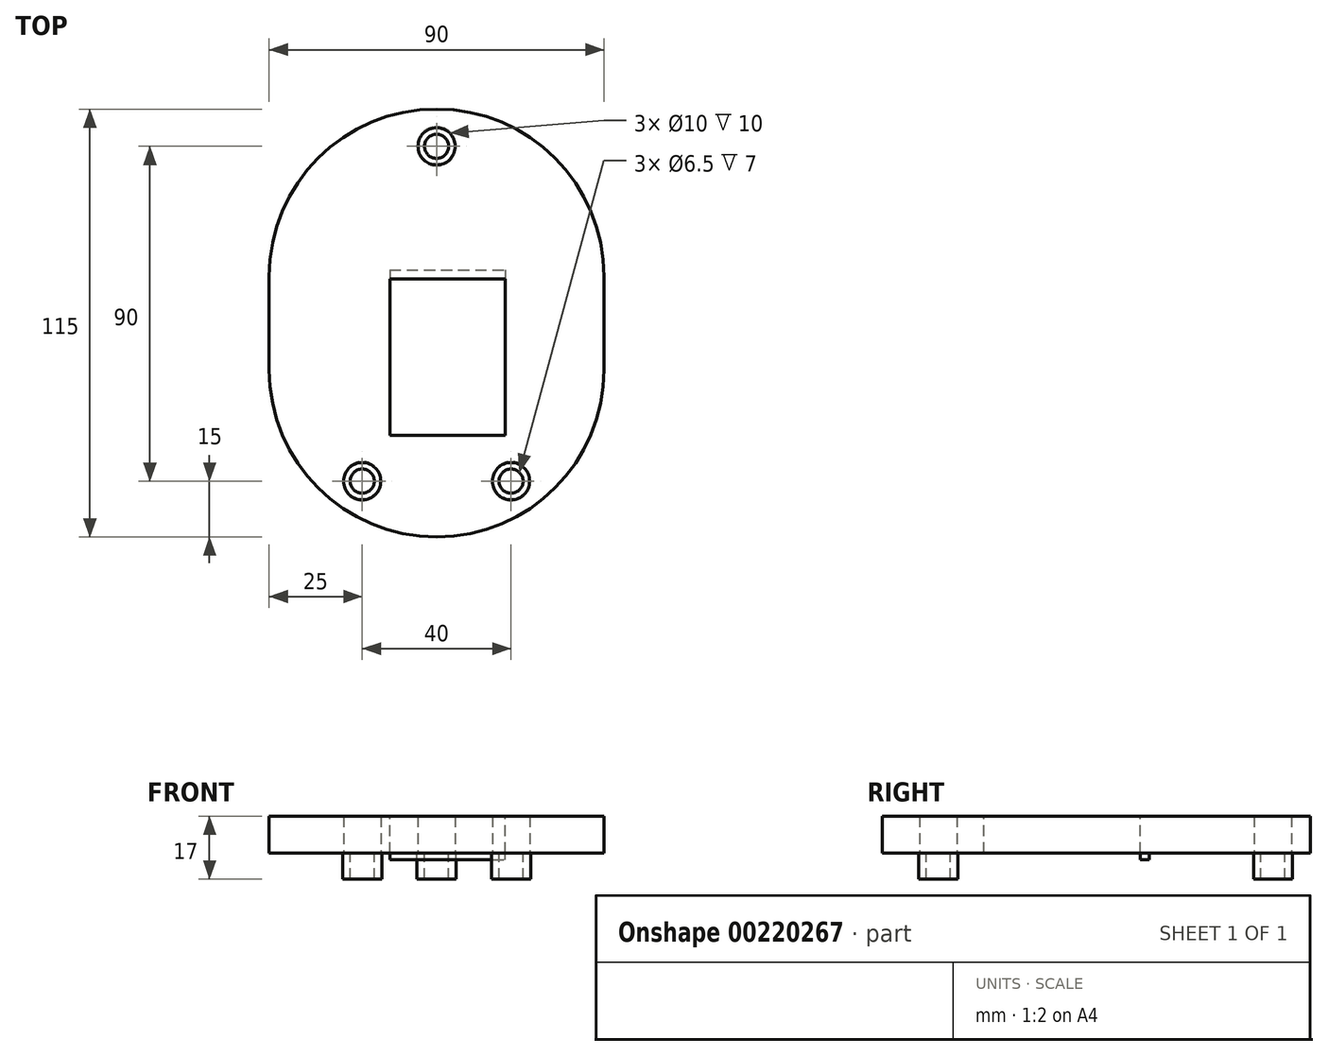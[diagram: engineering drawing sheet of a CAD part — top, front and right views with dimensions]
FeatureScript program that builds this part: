
annotation { "Feature Type Name" : "Feature", "Feature Type Description" : "" }
export const myFeature = defineFeature(function(context is Context, id is Id, definition is map)
    precondition{}
    {
        {
            var Q0;
            Q0=qCreatedBy(makeId("Top.planeOp"),FACE);
            var sketch = newSketch(context, id + "F0", { "sketchPlane" : qUnion([Q0])});
            skArc(sketch, "E0", {"start": v(-45, 0) * mm, "mid": v(0, -45) * mm, "end": v(45, 0) * mm});
            skLineSegment(sketch, "E1", {"start": v(-45, 0) * mm, "end": v(-45, 70) * mm});
            skLineSegment(sketch, "E2", {"start": v(-45, 70) * mm, "end": v(45, 70) * mm});
            skLineSegment(sketch, "E3", {"start": v(45, 70) * mm, "end": v(45, 0) * mm});
            skSolve(sketch);
        }
        {
            var Q0;
            Q0=qSketchRegion(id+"F0",true);
            extrude(context, id + "F1", {"entities" : qUnion([Q0]), "depth" : 10 * mm});
        }
        {
            var Q0;
            Q0=makeQuery(id+"F1.opExtrude","CAP_FACE",FACE,{"disambiguationData":[OSD([sQuery(id+"F0.wireOp",EDGE,"E0")])],"isStart":true});
            var sketch = newSketch(context, id + "F2", { "sketchPlane" : qUnion([Q0])});
            skCircle(sketch, "E4", {"center": v(0, 0) * mm, "radius": 9.5 * mm});
            skSolve(sketch);
        }
        {
            var Q0;
            Q0=makeQuery(id+"F1.opExtrude","SWEPT_EDGE",EDGE,{"disambiguationData":[OSD([sQuery(id+"F0.wireOp",EDGE,"E1"),sQuery(id+"F0.wireOp",EDGE,"E2")])]});
            var Q1;
            Q1=makeQuery(id+"F1.opExtrude","SWEPT_EDGE",EDGE,{"disambiguationData":[OSD([sQuery(id+"F0.wireOp",EDGE,"E2"),sQuery(id+"F0.wireOp",EDGE,"E3")])]});
            fillet(context, id + "F3", {"entities" : qUnion([Q0, Q1]), "radius" : 45 * mm, "tangentPropagation" : true, "allowEdgeOverflow" : false});
        }
        {
            var Q0;
            Q0=makeQuery(id+"F1.opExtrude","CAP_FACE",FACE,{"disambiguationData":[OSD([sQuery(id+"F0.wireOp",EDGE,"E0"),sQuery(id+"F0.wireOp",EDGE,"E1"),sQuery(id+"F0.wireOp",EDGE,"E2"),sQuery(id+"F0.wireOp",EDGE,"E3")])],"isStart":false});
            var sketch = newSketch(context, id + "F4", { "sketchPlane" : qUnion([Q0])});
            skLineSegment(sketch, "E5.bottom", {"start": v(-12.6, 24.3) * mm, "end": v(18.4, 24.3) * mm});
            skLineSegment(sketch, "E5.top", {"start": v(-12.6, -17.7) * mm, "end": v(18.4, -17.7) * mm});
            skLineSegment(sketch, "E5.left", {"start": v(-12.6, 24.3) * mm, "end": v(-12.6, -17.7) * mm});
            skLineSegment(sketch, "E5.right", {"start": v(18.4, 24.3) * mm, "end": v(18.4, -17.7) * mm});
            skSolve(sketch);
        }
        {
            var Q0;
            Q0=makeQuery(id+"F4.imprint","IMPRINT",FACE,{"disambiguationData":[TD([[makeQuery(id+"F4.imprint","IMPRINT",EDGE,{"derivedFrom":sQuery(id+"F4.wireOp",EDGE,"E5.bottom")}),-1.0]])]});
            extrude(context, id + "F5", {"entities" : qUnion([Q0]), "operationType" : NewBodyOperationType.REMOVE, "oppositeDirection" : true, "depth" : 11 * mm});
        }
        {
            var Q0;
            Q0=makeQuery(id+"F2.imprint","IMPRINT",FACE,{"disambiguationData":[TD([[makeQuery(id+"F2.imprint","IMPRINT",EDGE,{"derivedFrom":sQuery(id+"F2.wireOp",EDGE,"E4")}),-1.0]])]});
            var sketch = newSketch(context, id + "F6", { "sketchPlane" : qUnion([Q0])});
            skPoint(sketch, "E6", {"position": v(20, 30) * mm});
            skPoint(sketch, "E7", {"position": v(-20, 30) * mm});
            skPoint(sketch, "E8", {"position": v(0, -60) * mm});
            skCircle(sketch, "E9", {"center": v(0, -60) * mm, "radius": 5.25 * mm});
            skCircle(sketch, "E10", {"center": v(20, 30) * mm, "radius": 5.25 * mm});
            skCircle(sketch, "E11", {"center": v(-20, 30) * mm, "radius": 5.25 * mm});
            skSolve(sketch);
        }
        {
            var Q0;
            Q0=makeQuery(id+"F6.imprint","IMPRINT",FACE,{"disambiguationData":[TD([[makeQuery(id+"F6.imprint","IMPRINT",EDGE,{"derivedFrom":sQuery(id+"F6.wireOp",EDGE,"E9")}),1.0]])]});
            var Q1;
            Q1=makeQuery(id+"F6.imprint","IMPRINT",FACE,{"disambiguationData":[TD([[makeQuery(id+"F6.imprint","IMPRINT",EDGE,{"derivedFrom":sQuery(id+"F6.wireOp",EDGE,"E11")}),1.0]])]});
            var Q2;
            Q2=makeQuery(id+"F6.imprint","IMPRINT",FACE,{"disambiguationData":[TD([[makeQuery(id+"F6.imprint","IMPRINT",EDGE,{"derivedFrom":sQuery(id+"F6.wireOp",EDGE,"E10")}),1.0]])]});
            extrude(context, id + "F7", {"entities" : qUnion([Q0, Q1, Q2]), "operationType" : NewBodyOperationType.ADD, "depth" : 7 * mm});
        }
        {
            var Q0;
            Q0=makeQuery(id+"F1.opExtrude","CAP_FACE",FACE,{"disambiguationData":[OSD([sQuery(id+"F0.wireOp",EDGE,"E0"),sQuery(id+"F0.wireOp",EDGE,"E1"),sQuery(id+"F0.wireOp",EDGE,"E2"),sQuery(id+"F0.wireOp",EDGE,"E3")])],"isStart":true});
            var sketch = newSketch(context, id + "F8", { "sketchPlane" : qUnion([Q0])});
            skPoint(sketch, "E12", {"position": v(0, -60) * mm});
            skPoint(sketch, "E13", {"position": v(20, 30) * mm});
            skPoint(sketch, "E14", {"position": v(-20, 30) * mm});
            skCircle(sketch, "E15", {"center": v(-20, 30) * mm, "radius": 5 * mm});
            skCircle(sketch, "E16", {"center": v(20, 30) * mm, "radius": 5 * mm});
            skCircle(sketch, "E17", {"center": v(0, -60) * mm, "radius": 5 * mm});
            skSolve(sketch);
        }
        {
            var Q0;
            Q0=sQuery(id+"F8.wireOp",VERTEX,"E14");
            var Q1;
            Q1=sQuery(id+"F8.wireOp",VERTEX,"E13");
            var Q2;
            Q2=sQuery(id+"F8.wireOp",VERTEX,"E12");
            var Q3;
            Q3=makeQuery(id+"F1.opExtrude","SWEPT_BODY",BODY,{"disambiguationData":[OSD([sQuery(id+"F0.wireOp",EDGE,"E0"),sQuery(id+"F0.wireOp",EDGE,"E1"),sQuery(id+"F0.wireOp",EDGE,"E2"),sQuery(id+"F0.wireOp",EDGE,"E3")])]});
            hole(context, id + "F9", {"style" : HoleStyle.SIMPLE, "endStyle" : HoleEndStyle.THROUGH, "holeDiameter" : 10 * mm, "locations" : qUnion([Q0, Q1, Q2]), "scope" : qUnion([Q3]), "isTappedThrough" : true});
        }
        {
            var Q0;
            Q0=sQuery(id+"F8.wireOp",VERTEX,"E13");
            var Q1;
            Q1=sQuery(id+"F8.wireOp",VERTEX,"E12");
            var Q2;
            Q2=sQuery(id+"F6.wireOp",VERTEX,"E7");
            var Q3;
            Q3=makeQuery(id+"F1.opExtrude","SWEPT_BODY",BODY,{"disambiguationData":[OSD([sQuery(id+"F0.wireOp",EDGE,"E0"),sQuery(id+"F0.wireOp",EDGE,"E1"),sQuery(id+"F0.wireOp",EDGE,"E2"),sQuery(id+"F0.wireOp",EDGE,"E3")])]});
            hole(context, id + "F10", {"style" : HoleStyle.SIMPLE, "endStyle" : HoleEndStyle.THROUGH, "oppositeDirection" : true, "holeDiameter" : 6.5 * mm, "locations" : qUnion([Q0, Q1, Q2]), "scope" : qUnion([Q3]), "isTappedThrough" : true});
        }
        {
            var Q0;
            {var subQ3=sQuery(id+"F0.wireOp",EDGE,"E0");Q0=makeQuery(id+"F8.imprint","IMPRINT",FACE,{"disambiguationData":[TD([[makeQuery(id+"F8.imprint","IMPRINT",EDGE,{"derivedFrom":makeQuery(id+"F1.opExtrude","CAP_EDGE",EDGE,{"disambiguationData":[OSD([subQ3])],"isStart":true})}),-1.0]])]});}
            var sketch = newSketch(context, id + "F11", { "sketchPlane" : qUnion([Q0])});
            skLineSegment(sketch, "E18.bottom", {"start": v(-12.6, -26.8) * mm, "end": v(18.4, -26.8) * mm});
            skLineSegment(sketch, "E18.top", {"start": v(-12.6, -24.3) * mm, "end": v(18.4, -24.3) * mm});
            skLineSegment(sketch, "E18.left", {"start": v(-12.6, -26.8) * mm, "end": v(-12.6, -24.3) * mm});
            skLineSegment(sketch, "E18.right", {"start": v(18.4, -26.8) * mm, "end": v(18.4, -24.3) * mm});
            skSolve(sketch);
        }
        {
            var Q0;
            Q0=makeQuery(id+"F11.imprint","IMPRINT",FACE,{"disambiguationData":[TD([[makeQuery(id+"F11.imprint","IMPRINT",EDGE,{"derivedFrom":sQuery(id+"F11.wireOp",EDGE,"E18.bottom")}),1.0]])]});
            extrude(context, id + "F12", {"entities" : qUnion([Q0]), "operationType" : NewBodyOperationType.ADD, "depth" : 1.7 * mm});
        }
    });
